# Revit family: Butcher-Block_L-Shaped
name_source: partatom
category: Casework
units: mm (PartAtom-declared; Revit-internal decimal feet)

## family parameters
Always vertical = Yes
Classification Number = 23.40.70.17.21.11
Cut with Voids When Loaded = No
Room Calculation Point = No
Shared = No
Work Plane-Based = No

## types (1)
- Custom Fabricated
    Assembly Code = C1030400
    Construction Details = http://www.arcat.com
    Cost = 3050.09 $
    Default Elevation = 0' - 0"
    Description = Butcher Block Countertop - L Shaped
    Edge Cost_per Inch = 1
    Edge Type = Bevel : 1/2"
    Expected Lifespan (Years) = 30
    Finish = Tung Oil Polish
    Green Building-LEED = http://www.arcat.com
    Keynote = 06415
    Maintenance Schedule (Months) = 12
    Manufacturer = Generic
    Manufacturer Fax = (203) 939-2444
    Manufacturer Website = http://www.arcat.com
    Maximum Depth = 16' - 0"
    Maximum Length = 16' - 0"
    Model = Generic
    Product Data = http://www.arcat.com
    Product Properties = http://www.arcat.com
    Specification = http://www.arcat.com
    Sqft Cost = 71
    Warranty Duration (Years) = 15
    Width = 6' - 0"
    Wood Type 1 = Counter Material - Wood 2
    Wood Type 2 = Counter Material - Wood

## geometry (parser evidence)
native form markers: Sweep x5
no freeform markers — native parametric forms only
